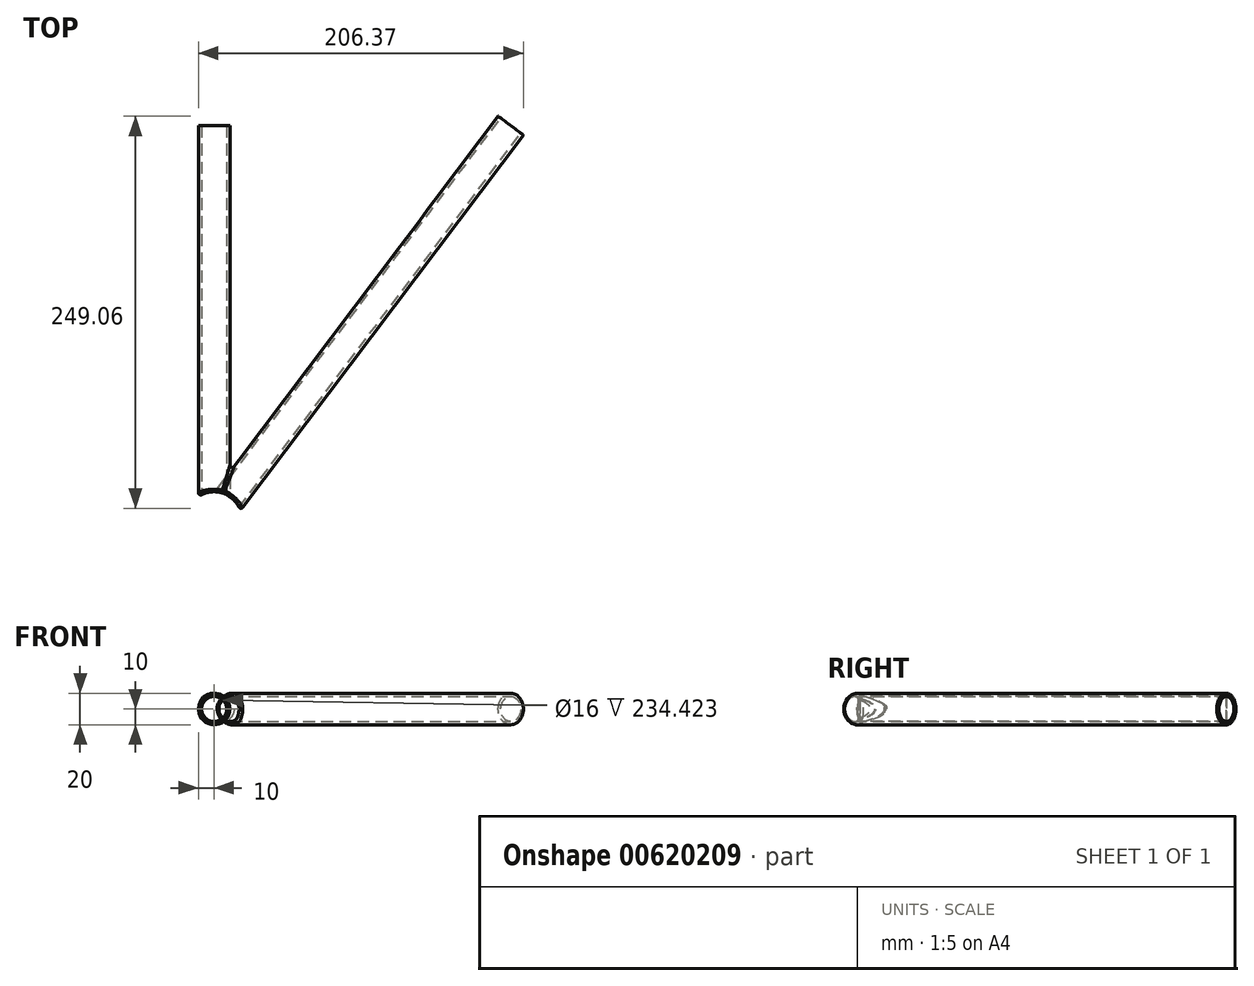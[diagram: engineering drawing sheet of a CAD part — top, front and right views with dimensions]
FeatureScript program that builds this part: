
annotation { "Feature Type Name" : "Feature", "Feature Type Description" : "" }
export const myFeature = defineFeature(function(context is Context, id is Id, definition is map)
    precondition{}
    {
        {
            var Q0;
            Q0=qCreatedBy(makeId("Top.planeOp"),FACE);
            var sketch = newSketch(context, id + "F0", { "sketchPlane" : qUnion([Q0])});
            skLineSegment(sketch, "E0", {"start": v(0, 0) * mm, "end": v(0, 250) * mm, "construction": true});
            skLineSegment(sketch, "E1", {"start": v(0, 0) * mm, "end": v(188.39, 250) * mm, "construction": true});
            skLineSegment(sketch, "E2", {"start": v(188.39, 250) * mm, "end": v(0, 250) * mm, "construction": true});
            skCircle(sketch, "E3", {"center": v(0, 0) * mm, "radius": 17.5 * mm, "construction": true});
            skSolve(sketch);
        }
        {
            var Q0;
            Q0=qCreatedBy(makeId("Right.planeOp"),FACE);
            var sketch = newSketch(context, id + "F1", { "sketchPlane" : qUnion([Q0])});
            skLineSegment(sketch, "E4", {"start": v(-17.5, 10) * mm, "end": v(-17.5, -10) * mm});
            skLineSegment(sketch, "E5", {"start": v(-17.5, -10) * mm, "end": v(-13.5, -10) * mm});
            skLineSegment(sketch, "E6", {"start": v(-13.5, -10) * mm, "end": v(-13.5, -8) * mm});
            skLineSegment(sketch, "E7", {"start": v(-13.5, -8) * mm, "end": v(-15, -8) * mm});
            skLineSegment(sketch, "E8", {"start": v(-15, -8) * mm, "end": v(-15, 8) * mm});
            skLineSegment(sketch, "E9", {"start": v(-15, 8) * mm, "end": v(-16, 8) * mm});
            skLineSegment(sketch, "E10", {"start": v(-16, 8) * mm, "end": v(-16, 9) * mm});
            skLineSegment(sketch, "E11", {"start": v(-16, 9) * mm, "end": v(-15, 9) * mm});
            skLineSegment(sketch, "E12", {"start": v(-15, 9) * mm, "end": v(-15, 10) * mm});
            skLineSegment(sketch, "E13", {"start": v(-15, 10) * mm, "end": v(-17.5, 10) * mm});
            skLineSegment(sketch, "E14", {"start": v(0, 0) * mm, "end": v(-15, 0) * mm});
            skLineSegment(sketch, "E15", {"start": v(0, 0) * mm, "end": v(0, 7) * mm, "construction": true});
            skLineSegment(sketch, "E16", {"start": v(-15, 0) * mm, "end": v(-17.5, 0) * mm, "construction": true});
            skSolve(sketch);
        }
        {
            var Q0;
            Q0=makeQuery(id+"F1.imprint","IMPRINT",FACE,{"disambiguationData":[TD([[makeQuery(id+"F1.imprint","IMPRINT",EDGE,{"derivedFrom":sQuery(id+"F1.wireOp",EDGE,"E4")}),1.0]])]});
            var Q1;
            Q1=sQuery(id+"F1.wireOp",EDGE,"E15");
            revolve(context, id + "F2", {"entities" : qUnion([Q0]), "axis" : qUnion([Q1]), "revolveType" : RevolveType.FULL});
        }
        {
            var Q0;
            Q0=qCreatedBy(makeId("Front.planeOp"),FACE);
            var sketch = newSketch(context, id + "F3", { "sketchPlane" : qUnion([Q0])});
            skCircle(sketch, "E17", {"center": v(0, 0) * mm, "radius": 10 * mm});
            skCircle(sketch, "E18", {"center": v(0, 0) * mm, "radius": 8 * mm});
            skSolve(sketch);
        }
        {
            var Q0;
            Q0=qSketchRegion(id+"F3",true);
            var Q1;
            Q1=sQuery(id+"F0.wireOp",VERTEX,"E2.end");
            extrude(context, id + "F4", {"entities" : qUnion([Q0]), "endBound" : BoundingType.UP_TO_VERTEX, "oppositeDirection" : true, "depth" : 25 * mm, "endBoundEntityVertex" : qUnion([Q1]), "offsetDistance" : 25 * mm});
        }
        {
            var Q0;
            Q0=qCreatedBy(makeId("Top.planeOp"),FACE);
            var sketch = newSketch(context, id + "F5", { "sketchPlane" : qUnion([Q0])});
            skCircle(sketch, "E19", {"center": v(0, 0) * mm, "radius": 17.5 * mm});
            skSolve(sketch);
        }
        {
            var Q0;
            Q0=qSketchRegion(id+"F5",true);
            extrude(context, id + "F6", {"entities" : qUnion([Q0]), "operationType" : NewBodyOperationType.REMOVE, "endBound" : BoundingType.SYMMETRIC, "oppositeDirection" : true, "depth" : 25 * mm, "offsetDistance" : 25 * mm});
        }
        {
            var Q0;
            Q0=qCreatedBy(makeId("Top.planeOp"),FACE);
            var sketch = newSketch(context, id + "F7", { "sketchPlane" : qUnion([Q0])});
            skLineSegment(sketch, "E20", {"start": v(0, 0) * mm, "end": v(7.99, -6.02) * mm, "construction": true});
            skLineSegment(sketch, "E21", {"start": v(7.99, -6.02) * mm, "end": v(196.37, 243.98) * mm});
            skLineSegment(sketch, "E22", {"start": v(196.37, 243.98) * mm, "end": v(188.39, 250) * mm, "construction": true});
            skLineSegment(sketch, "E23", {"start": v(188.39, 250) * mm, "end": v(0, 0) * mm, "construction": true});
            skLineSegment(sketch, "E24", {"start": v(6.39, -4.81) * mm, "end": v(194.78, 245.19) * mm});
            skLineSegment(sketch, "E25", {"start": v(6.39, -4.81) * mm, "end": v(7.99, -6.02) * mm});
            skLineSegment(sketch, "E26", {"start": v(194.78, 245.19) * mm, "end": v(196.37, 243.98) * mm});
            skSolve(sketch);
        }
        {
            var Q0;
            Q0=makeQuery(id+"F7.imprint","IMPRINT",FACE,{"disambiguationData":[TD([[makeQuery(id+"F7.imprint","IMPRINT",EDGE,{"derivedFrom":sQuery(id+"F7.wireOp",EDGE,"E21")}),1.0]])]});
            var Q1;
            Q1=sQuery(id+"F7.wireOp",EDGE,"E23");
            revolve(context, id + "F8", {"entities" : qUnion([Q0]), "axis" : qUnion([Q1]), "revolveType" : RevolveType.FULL});
        }
        {
            var Q0;
            Q0=qSketchRegion(id+"F5",true);
            extrude(context, id + "F9", {"entities" : qUnion([Q0]), "operationType" : NewBodyOperationType.REMOVE, "endBound" : BoundingType.SYMMETRIC, "oppositeDirection" : true, "depth" : 91.2 * mm, "offsetDistance" : 25 * mm});
        }
        {
            var Q0;
            Q0=makeQuery(id+"F2.opRevolve","SWEPT_BODY",BODY,{"disambiguationData":[OSD([sQuery(id+"F1.wireOp",EDGE,"E4"),sQuery(id+"F1.wireOp",EDGE,"E5"),sQuery(id+"F1.wireOp",EDGE,"E6"),sQuery(id+"F1.wireOp",EDGE,"E7"),sQuery(id+"F1.wireOp",EDGE,"E8"),sQuery(id+"F1.wireOp",EDGE,"E9"),sQuery(id+"F1.wireOp",EDGE,"E10"),sQuery(id+"F1.wireOp",EDGE,"E11"),sQuery(id+"F1.wireOp",EDGE,"E12"),sQuery(id+"F1.wireOp",EDGE,"E13")])]});
            var Q1;
            Q1=makeQuery(id+"F4.opExtrude","SWEPT_BODY",BODY,{"disambiguationData":[OSD([sQuery(id+"F3.wireOp",EDGE,"E17"),sQuery(id+"F3.wireOp",EDGE,"E18")])]});
            var Q2;
            Q2=makeQuery(id+"F8.opRevolve","SWEPT_BODY",BODY,{"disambiguationData":[OSD([sQuery(id+"F7.wireOp",EDGE,"E21"),sQuery(id+"F7.wireOp",EDGE,"E24"),sQuery(id+"F7.wireOp",EDGE,"E25"),sQuery(id+"F7.wireOp",EDGE,"E26")])]});
            booleanBodies(context, id + "F10", {"operationType" : BooleanOperationType.UNION, "tools" : qUnion([Q0, Q1, Q2])});
        }
        {
            var Q0;
            {var subQ0=makeQuery(id+"F8.opRevolve","SWEPT_FACE",FACE,{"disambiguationData":[OSD([sQuery(id+"F7.wireOp",EDGE,"E21")])]});Q0=makeQuery(id+"F10.opBoolean","SPLIT",EDGE,{"disambiguationData":[TD([makeQuery(id+"F2.opRevolve","SWEPT_FACE",FACE,{"disambiguationData":[OSD([sQuery(id+"F1.wireOp",EDGE,"E4")])]}),makeQuery(id+"F2.opRevolve","SWEPT_FACE",FACE,{"disambiguationData":[OSD([sQuery(id+"F1.wireOp",EDGE,"E5")])]}),makeQuery(id+"F2.opRevolve","SWEPT_FACE",FACE,{"disambiguationData":[OSD([sQuery(id+"F1.wireOp",EDGE,"E13")])]}),subQ0])],"derivedFrom":makeQuery(id+"F9.boolean.opBoolean","INTERSECT",EDGE,{"derivedFrom":[subQ0,makeQuery(id+"F9.opExtrude","SWEPT_FACE",FACE,{"disambiguationData":[OSD([sQuery(id+"F5.wireOp",EDGE,"E19")])]})]})});}
            var Q1;
            {var subQ0=makeQuery(id+"F4.opExtrude","SWEPT_FACE",FACE,{"disambiguationData":[OSD([sQuery(id+"F3.wireOp",EDGE,"E17")])]});Q1=makeQuery(id+"F10.opBoolean","SPLIT",EDGE,{"disambiguationData":[TD([makeQuery(id+"F2.opRevolve","SWEPT_FACE",FACE,{"disambiguationData":[OSD([sQuery(id+"F1.wireOp",EDGE,"E4")])]}),makeQuery(id+"F2.opRevolve","SWEPT_FACE",FACE,{"disambiguationData":[OSD([sQuery(id+"F1.wireOp",EDGE,"E13")])]}),subQ0,makeQuery(id+"F8.opRevolve","SWEPT_FACE",FACE,{"disambiguationData":[OSD([sQuery(id+"F7.wireOp",EDGE,"E21")])]})])],"derivedFrom":makeQuery(id+"F6.boolean.opBoolean","INTERSECT",EDGE,{"derivedFrom":[subQ0,makeQuery(id+"F6.opExtrude","SWEPT_FACE",FACE,{"disambiguationData":[OSD([sQuery(id+"F5.wireOp",EDGE,"E19")])]})]})});}
            var Q2;
            Q2=makeQuery(id+"F10.opBoolean","INTERSECT",EDGE,{"derivedFrom":[makeQuery(id+"F4.opExtrude","SWEPT_FACE",FACE,{"disambiguationData":[OSD([sQuery(id+"F3.wireOp",EDGE,"E17")])]}),makeQuery(id+"F8.opRevolve","SWEPT_FACE",FACE,{"disambiguationData":[OSD([sQuery(id+"F7.wireOp",EDGE,"E21")])]})]});
            var Q3;
            {var subQ0=makeQuery(id+"F4.opExtrude","SWEPT_FACE",FACE,{"disambiguationData":[OSD([sQuery(id+"F3.wireOp",EDGE,"E17")])]});Q3=makeQuery(id+"F10.opBoolean","SPLIT",EDGE,{"disambiguationData":[TD([makeQuery(id+"F2.opRevolve","SWEPT_FACE",FACE,{"disambiguationData":[OSD([sQuery(id+"F1.wireOp",EDGE,"E4")])]}),makeQuery(id+"F2.opRevolve","SWEPT_FACE",FACE,{"disambiguationData":[OSD([sQuery(id+"F1.wireOp",EDGE,"E5")])]}),makeQuery(id+"F2.opRevolve","SWEPT_FACE",FACE,{"disambiguationData":[OSD([sQuery(id+"F1.wireOp",EDGE,"E13")])]}),subQ0])],"derivedFrom":makeQuery(id+"F6.boolean.opBoolean","INTERSECT",EDGE,{"derivedFrom":[subQ0,makeQuery(id+"F6.opExtrude","SWEPT_FACE",FACE,{"disambiguationData":[OSD([sQuery(id+"F5.wireOp",EDGE,"E19")])]})]})});}
            fillet(context, id + "F11", {"entities" : qUnion([Q0, Q1, Q2, Q3]), "radius" : 1.5 * mm, "tangentPropagation" : true, "allowEdgeOverflow" : false});
        }
    });
